# Revit family: Plumbing Fixture_WallgateWallgate_Wall_Cistern_Multiple_CIST19-PNEU-2_W
name_source: partatom
category: Plumbing Fixtures
revit_build: Autodesk Revit 2017 (Build: 20160225_1515(x64)
units: mm (PartAtom-declared; Revit-internal decimal feet)

## family parameters
Always vertical = No
Cut with Voids When Loaded = No
Part Type = Normal
Room Calculation Point = No
Round Connector Dimension = Use Diameter
Shared = No
Work Plane-Based = Yes

## types (1)
- Type 1
    Anti-Ligature = no
    Application = Commercial
    CW Connection = Yes
    Category/StyleorType_ANZRS = Plumbing Fixture
    Cold Water = Yes
    DataSheet = https://www.galvinengineering.com.au
    Description = Wallgate Pneumatic Activated Concealed Slim - Line 4.5L & 6L Cistern Only Single Flush
    Height = 0 mm  [stored 0 ft]
    Hot Water = No
    Instructions = https://www.galvinengineering.com.au
    Manufacturer = Wallgate
    Manufacturer_Overall Depth = 0 mm  [stored 0 ft]
    Manufacturer_Overall Height = 0 mm  [stored 0 ft]
    Manufacturer_Overall Width = 0 mm  [stored 0 ft]
    Mounting = Wall
    Mounting Surface = Wall
    Product Range (Series) = Wallgate
    Product Type = Cistern
    SKU = CIST19-PNEU-2
    Specify Host = Face
    Thread = 1/2" BSP M
    URL = http://www.galvinengineering.com.au
    Vandal Resistant = no
    Variants = -

note: [stored X ft] marks values corroborated as IEEE doubles in the binary element streams (Revit-internal decimal feet)

## geometry (parser evidence)
native form markers: Sweep x9
no freeform markers — native parametric forms only
